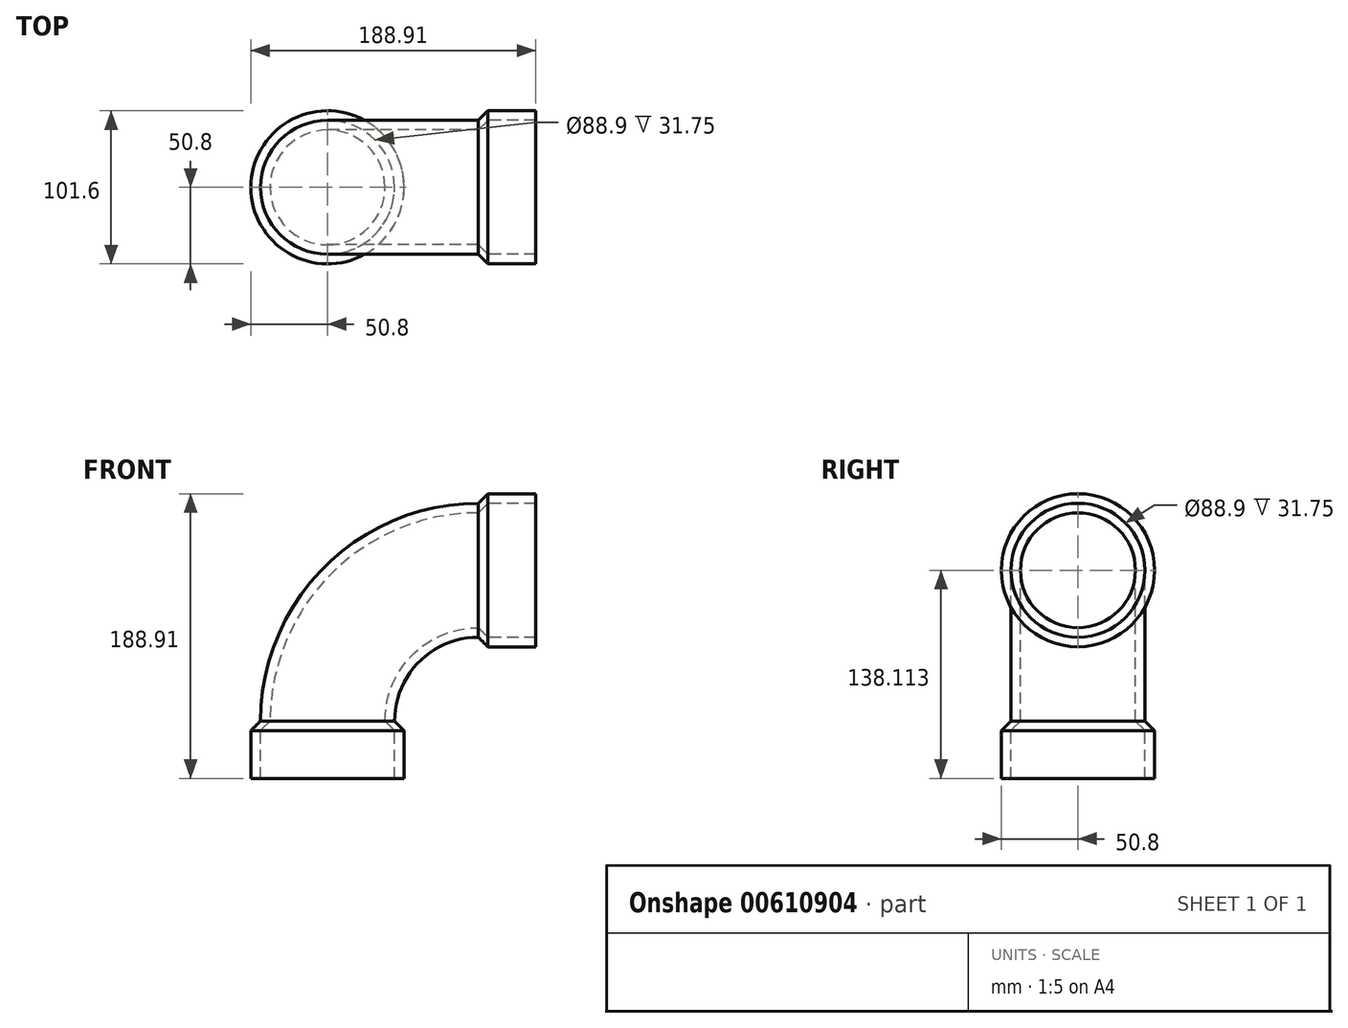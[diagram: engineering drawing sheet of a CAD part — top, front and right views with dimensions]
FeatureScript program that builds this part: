
annotation { "Feature Type Name" : "Feature", "Feature Type Description" : "" }
export const myFeature = defineFeature(function(context is Context, id is Id, definition is map)
    precondition{}
    {
        {
            var Q0;
            Q0=qCreatedBy(makeId("Top.planeOp"),FACE);
            var sketch = newSketch(context, id + "F0", { "sketchPlane" : qUnion([Q0])});
            skCircle(sketch, "E0", {"center": v(0, 0) * mm, "radius": 44.45 * mm});
            skCircle(sketch, "E1", {"center": v(0, 0) * mm, "radius": 38.1 * mm});
            skSolve(sketch);
        }
        {
            var Q0;
            Q0=qCreatedBy(makeId("Front.planeOp"),FACE);
            var sketch = newSketch(context, id + "F1", { "sketchPlane" : qUnion([Q0])});
            skArc(sketch, "E2", {"start": v(0, 0) * mm, "mid": v(29.3, 70.72) * mm, "end": v(100.01, 100.01) * mm});
            skSolve(sketch);
        }
        {
            var Q0;
            Q0=makeQuery(id+"F0.imprint","IMPRINT",FACE,{"disambiguationData":[TD([[makeQuery(id+"F0.imprint","IMPRINT",EDGE,{"derivedFrom":sQuery(id+"F0.wireOp",EDGE,"E0")}),1.0]])]});
            var Q1;
            Q1=sQuery(id+"F1.wireOp",EDGE,"E2");
            sweep(context, id + "F2", {"profiles" : qUnion([Q0]), "path" : qUnion([Q1])});
        }
        {
            var Q0;
            Q0=makeQuery(id+"F2.opSweep","CAP_FACE",FACE,{"disambiguationData":[OSD([sQuery(id+"F0.wireOp",EDGE,"E0"),sQuery(id+"F0.wireOp",EDGE,"E1"),sQuery(id+"F1.wireOp",VERTEX,"E2.end")])],"isStart":false});
            var sketch = newSketch(context, id + "F3", { "sketchPlane" : qUnion([Q0])});
            skCircle(sketch, "E3", {"center": v(0, 100.01) * mm, "radius": 50.8 * mm});
            skCircle(sketch, "E4", {"center": v(0, 100.01) * mm, "radius": 44.45 * mm});
            skSolve(sketch);
        }
        {
            var Q0;
            Q0=makeQuery(id+"F2.opSweep","CAP_FACE",FACE,{"disambiguationData":[OSD([sQuery(id+"F0.wireOp",EDGE,"E0"),sQuery(id+"F0.wireOp",EDGE,"E1"),sQuery(id+"F1.wireOp",VERTEX,"E2.end")])],"isStart":false});
            extrude(context, id + "F4", {"entities" : qUnion([Q0]), "operationType" : NewBodyOperationType.ADD, "depth" : 6.35 * mm, "offsetDistance" : 25.4 * mm});
        }
        {
            var Q0;
            Q0=makeQuery(id+"F3.imprint","IMPRINT",FACE,{"disambiguationData":[TD([[makeQuery(id+"F3.imprint","IMPRINT",EDGE,{"derivedFrom":sQuery(id+"F3.wireOp",EDGE,"E3")}),1.0]])]});
            extrude(context, id + "F5", {"entities" : qUnion([Q0]), "operationType" : NewBodyOperationType.ADD, "depth" : 38.1 * mm, "offsetDistance" : 25.4 * mm});
        }
        {
            var Q0;
            Q0=makeQuery(id+"F2.opSweep","CAP_FACE",FACE,{"disambiguationData":[OSD([sQuery(id+"F0.wireOp",EDGE,"E0"),sQuery(id+"F0.wireOp",EDGE,"E1"),sQuery(id+"F1.wireOp",VERTEX,"E2.start")])],"isStart":true});
            var sketch = newSketch(context, id + "F6", { "sketchPlane" : qUnion([Q0])});
            skCircle(sketch, "E5", {"center": v(0, 0) * mm, "radius": 44.45 * mm});
            skCircle(sketch, "E6", {"center": v(0, 0) * mm, "radius": 50.8 * mm});
            skSolve(sketch);
        }
        {
            var Q0;
            Q0=makeQuery(id+"F2.opSweep","CAP_FACE",FACE,{"disambiguationData":[OSD([sQuery(id+"F0.wireOp",EDGE,"E0"),sQuery(id+"F0.wireOp",EDGE,"E1"),sQuery(id+"F1.wireOp",VERTEX,"E2.start")])],"isStart":true});
            extrude(context, id + "F7", {"entities" : qUnion([Q0]), "operationType" : NewBodyOperationType.ADD, "depth" : 6.35 * mm, "offsetDistance" : 25.4 * mm});
        }
        {
            var Q0;
            Q0=makeQuery(id+"F6.imprint","IMPRINT",FACE,{"disambiguationData":[TD([[makeQuery(id+"F6.imprint","IMPRINT",EDGE,{"derivedFrom":sQuery(id+"F6.wireOp",EDGE,"E5")}),1.0]])]});
            extrude(context, id + "F8", {"entities" : qUnion([Q0]), "operationType" : NewBodyOperationType.ADD, "depth" : 38.1 * mm, "offsetDistance" : 25.4 * mm});
        }
        {
            var Q0;
            Q0=makeQuery(id+"F5.opExtrude","CAP_EDGE",EDGE,{"disambiguationData":[OSD([sQuery(id+"F3.wireOp",EDGE,"E3")])],"isStart":true});
            var Q1;
            Q1=makeQuery(id+"F8.opExtrude","CAP_EDGE",EDGE,{"disambiguationData":[OSD([sQuery(id+"F6.wireOp",EDGE,"E6")])],"isStart":true});
            var Q2;
            Q2=makeQuery(id+"F4.opExtrude","CAP_EDGE",EDGE,{"disambiguationData":[OSD([sQuery(id+"F0.wireOp",EDGE,"E1"),sQuery(id+"F1.wireOp",VERTEX,"E2.end")])],"isStart":false});
            var Q3;
            Q3=makeQuery(id+"F7.opExtrude","CAP_EDGE",EDGE,{"disambiguationData":[OSD([sQuery(id+"F0.wireOp",EDGE,"E1"),sQuery(id+"F1.wireOp",VERTEX,"E2.start")])],"isStart":false});
            chamfer(context, id + "F9", {"entities" : qUnion([Q0, Q1, Q2, Q3]), "width" : 6.35 * mm, "tangentPropagation" : true});
        }
    });
